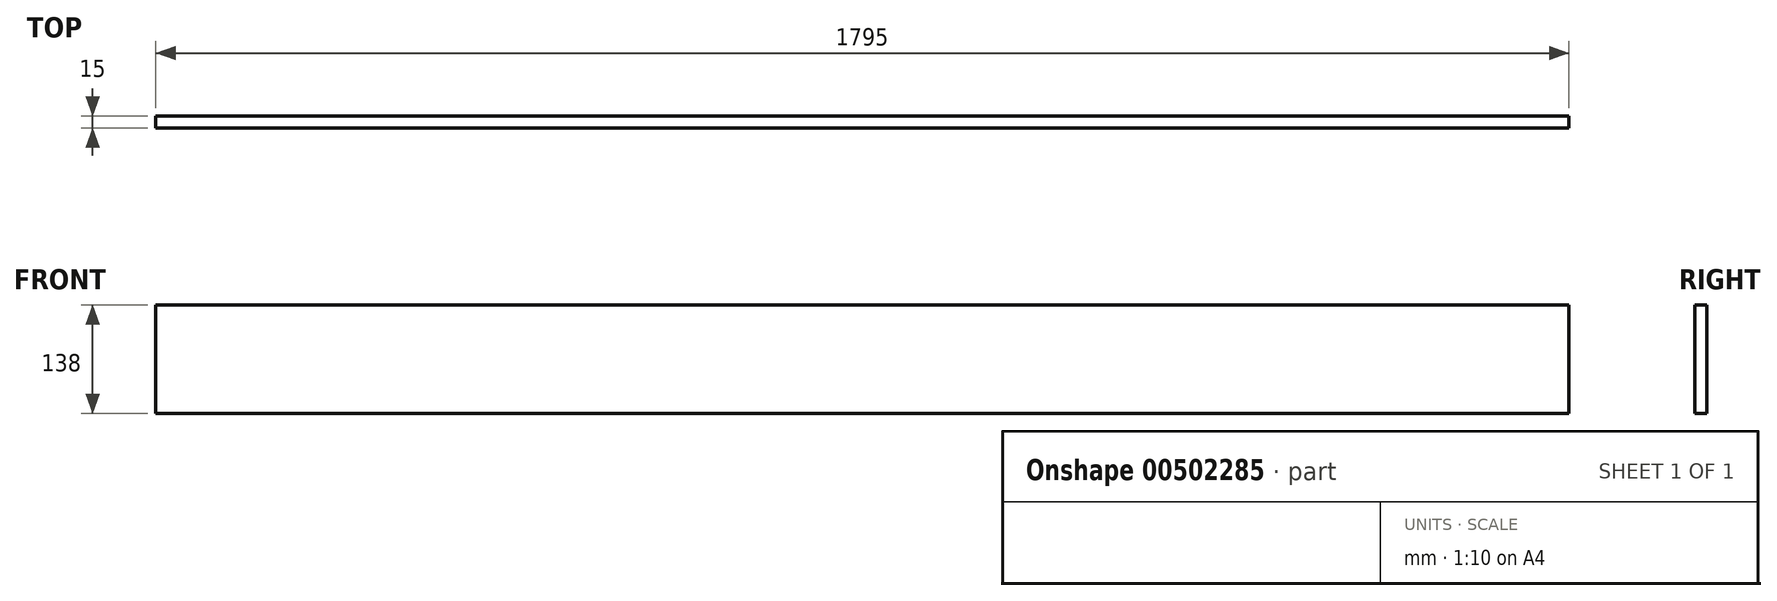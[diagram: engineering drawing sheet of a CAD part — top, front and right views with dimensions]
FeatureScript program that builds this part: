
annotation { "Feature Type Name" : "Feature", "Feature Type Description" : "" }
export const myFeature = defineFeature(function(context is Context, id is Id, definition is map)
    precondition{}
    {
        {
            var Q0;
            Q0=qCreatedBy(makeId("Front.planeOp"),FACE);
            var sketch = newSketch(context, id + "F0", { "sketchPlane" : qUnion([Q0])});
            skLineSegment(sketch, "E0.bottom", {"start": v(-1000, 69) * mm, "end": v(795, 69) * mm});
            skLineSegment(sketch, "E0.top", {"start": v(-1000, -69) * mm, "end": v(795, -69) * mm});
            skLineSegment(sketch, "E0.left", {"start": v(-1000, 69) * mm, "end": v(-1000, -69) * mm});
            skLineSegment(sketch, "E0.right", {"start": v(795, 69) * mm, "end": v(795, -69) * mm});
            skSolve(sketch);
        }
        {
            var Q0;
            Q0 = qSketchRegion(id + "F0", true);
            extrude(context, id + "F1", {"entities" : qUnion([Q0]), "depth" : 15 * mm});
        }
    });
